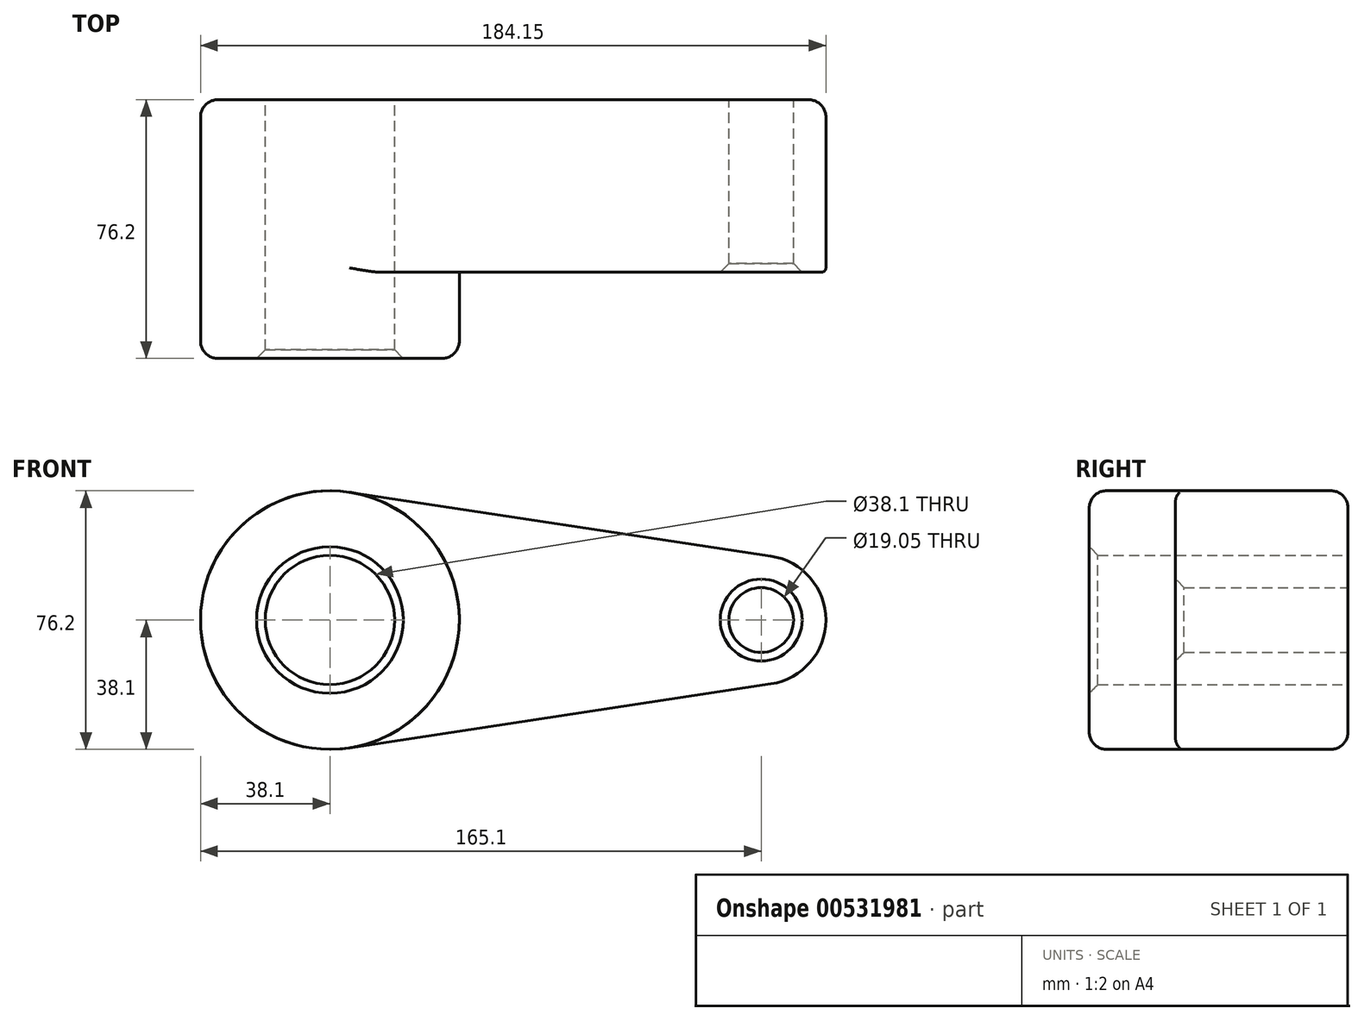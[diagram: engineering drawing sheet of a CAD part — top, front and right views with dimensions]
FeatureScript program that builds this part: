
annotation { "Feature Type Name" : "Feature", "Feature Type Description" : "" }
export const myFeature = defineFeature(function(context is Context, id is Id, definition is map)
    precondition{}
    {
        {
            var Q0;
            Q0=qCreatedBy(makeId("Front.planeOp"),FACE);
            var sketch = newSketch(context, id + "F0", { "sketchPlane" : qUnion([Q0])});
            skCircle(sketch, "E0", {"center": v(0, 0) * mm, "radius": 38.1 * mm});
            skCircle(sketch, "E1", {"center": v(127, 0) * mm, "radius": 19.05 * mm});
            skLineSegment(sketch, "E2", {"start": v(5.71, 37.67) * mm, "end": v(129.86, 18.83) * mm});
            skLineSegment(sketch, "E3", {"start": v(5.71, -37.67) * mm, "end": v(129.86, -18.83) * mm});
            skCircle(sketch, "E4", {"center": v(0, 0) * mm, "radius": 19.05 * mm});
            skCircle(sketch, "E5", {"center": v(127, 0) * mm, "radius": 9.53 * mm});
            skSolve(sketch);
        }
        {
            var Q0;
            Q0 = qSketchRegion(id + "F0", true);
            extrude(context, id + "F1", {"entities" : qUnion([Q0]), "depth" : 50.8 * mm, "offsetDistance" : 25.4 * mm});
        }
        {
            var Q0;
            Q0=makeQuery(id+"F0.imprint","IMPRINT",FACE,{"disambiguationData":[TD([[makeQuery(id+"F0.imprint","IMPRINT",EDGE,{"derivedFrom":sQuery(id+"F0.wireOp",EDGE,"E4")}),-1.0]])]});
            extrude(context, id + "F2", {"entities" : qUnion([Q0]), "operationType" : NewBodyOperationType.ADD, "depth" : 76.2 * mm, "offsetDistance" : 25.4 * mm});
        }
        {
            var Q0;
            Q0=makeQuery(id+"F1.opExtrude","CAP_EDGE",EDGE,{"disambiguationData":[OSD([sQuery(id+"F0.wireOp",EDGE,"E3")])],"isStart":true});
            var Q1;
            Q1=makeQuery(id+"F2.opExtrude","CAP_EDGE",EDGE,{"disambiguationData":[OSD([sQuery(id+"F0.wireOp",EDGE,"E0")])],"isStart":false});
            fillet(context, id + "F3", {"entities" : qUnion([Q0, Q1]), "radius" : 5.08 * mm, "tangentPropagation" : true, "allowEdgeOverflow" : false});
        }
        {
            var Q0;
            Q0=makeQuery(id+"F2.opExtrude","CAP_EDGE",EDGE,{"disambiguationData":[OSD([sQuery(id+"F0.wireOp",EDGE,"E4")])],"isStart":false});
            var Q1;
            Q1=makeQuery(id+"F1.opExtrude","CAP_EDGE",EDGE,{"disambiguationData":[OSD([sQuery(id+"F0.wireOp",EDGE,"E5")])],"isStart":false});
            chamfer(context, id + "F4", {"entities" : qUnion([Q0, Q1]), "width" : 2.54 * mm, "tangentPropagation" : true});
        }
        {
            var Q0;
            Q0=makeQuery(id+"F1.opExtrude","CAP_EDGE",EDGE,{"disambiguationData":[OSD([sQuery(id+"F0.wireOp",EDGE,"E3")])],"isStart":false});
            fillet(context, id + "F5", {"entities" : qUnion([Q0]), "radius" : 1.27 * mm, "tangentPropagation" : true, "allowEdgeOverflow" : false});
        }
    });
